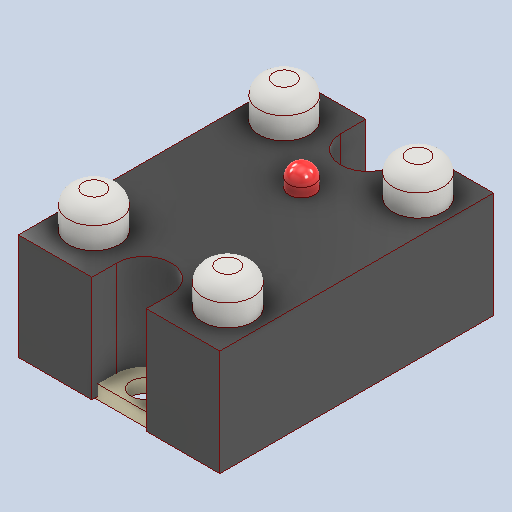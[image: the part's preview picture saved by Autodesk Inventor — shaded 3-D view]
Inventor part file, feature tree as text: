
AUTODESK INVENTOR PART (.ipt)
format: ipt  version: 2023 (Build 270158030, 158C)  size: 241,152 bytes
history: native  units: mm
features: other x10, sketch x4, plane x1
ambient origin geometry x8: Origin, YZ Plane, XZ Plane, XY Plane, X Axis, Y Axis, Z Axis, Center Point
bodies: Body1 (feature_tree), Body2 (feature_tree), Body3 (feature_tree), Body4 (feature_tree)
feature tree (15):
  other  "solid state relay.ipt"
  other  "plate::solid state relay.ipt"
  other  "case::solid state relay.ipt"
  other  "screw-terminals::solid state relay.ipt"
  other  "led::solid state relay.ipt"
  other  "TaggingFeature1"
  sketch  "Sketch1"  dims[d0=10.0mm]
  sketch  "Sketch2"
  sketch  "Sketch3"
  sketch  "Sketch4"
  plane  "Work Plane1"
  other  "plate"
  other  "case"
  other  "screw-terminals"
  other  "led"
